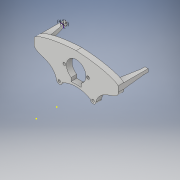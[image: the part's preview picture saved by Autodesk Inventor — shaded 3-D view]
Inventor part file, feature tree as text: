
AUTODESK INVENTOR PART (.ipt)
format: ipt  version: 2019 (Build 230136000, 136)  size: 201,216 bytes
history: native  units: mm
features: sketch x6, other x4, extrude x2, projected_geometry x2, loft x1, mirror x1
ambient origin geometry x8: Origin, YZ Plane, XZ Plane, XY Plane, X Axis, Y Axis, Z Axis, Center Point
bodies: Body1 (feature_tree)
feature tree (16):
  other  "Bryła1"
  sketch  "Szkic2"
  other  "Płaszczyzna konstrukcyjna1"
  other  "Płaszczyzna konstrukcyjna2"
  sketch  "Szkic3"
  extrude  "Wyciągnięcie proste1"  Depth=29.0mm
  sketch  "Szkic4"
  extrude  "Wyciągnięcie proste2"  Depth=4.5mm
  sketch  "Szkic6"
  sketch  "Szkic7"
  loft  "Wyciągnięcie złożone1"
  mirror  "Odbij1"
  projected_geometry  "Pętla rzutowana1"
  sketch  "Szkic5"
  projected_geometry  "Pętla rzutowana3"
  other  "Krawędzie1"
